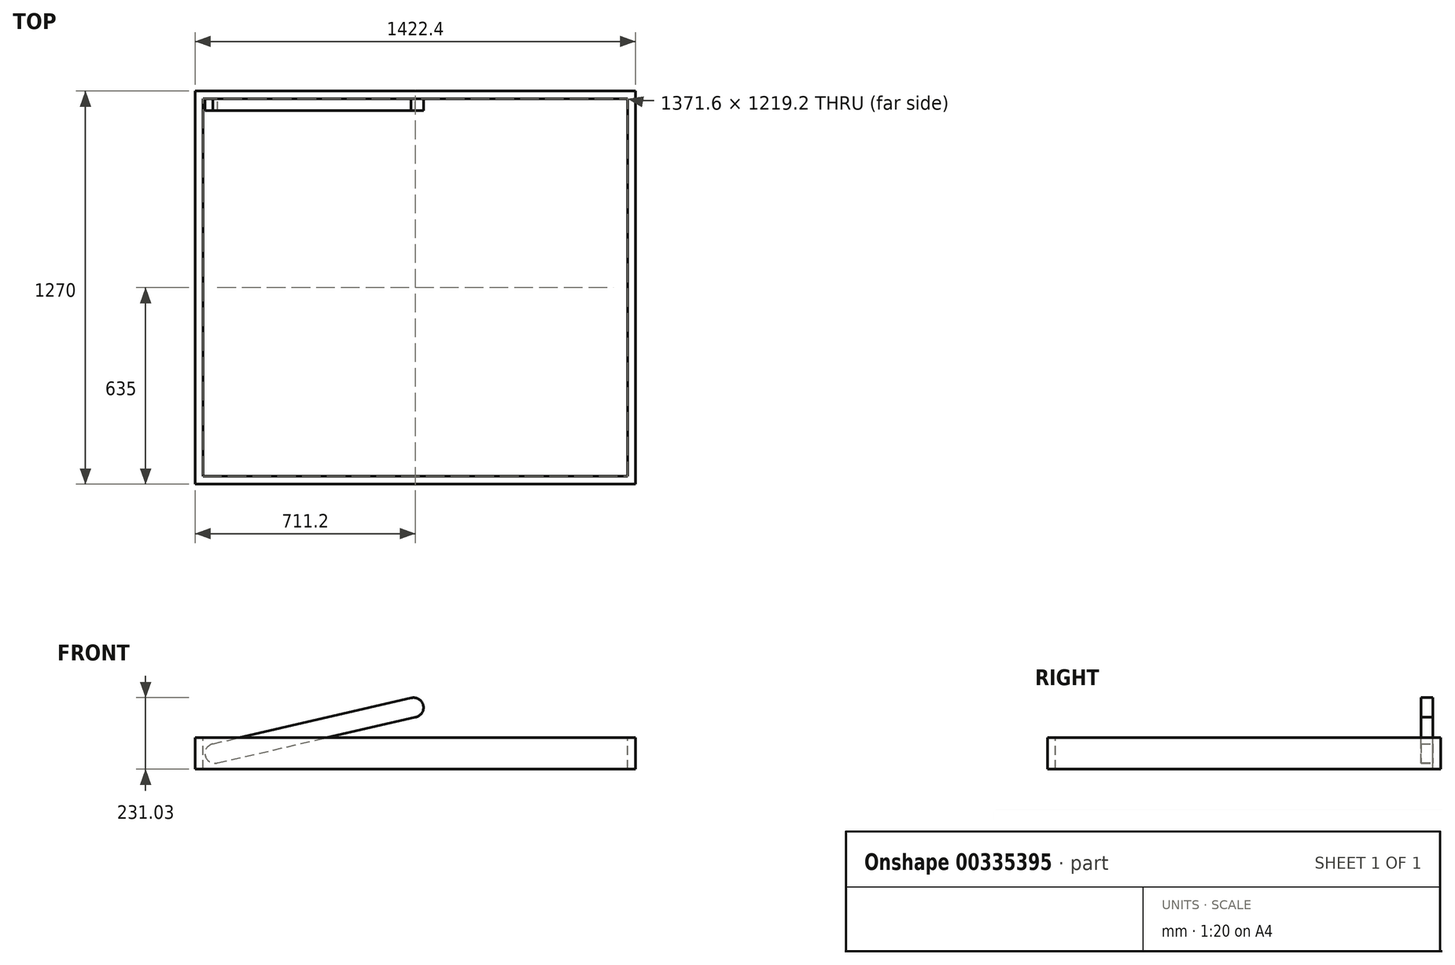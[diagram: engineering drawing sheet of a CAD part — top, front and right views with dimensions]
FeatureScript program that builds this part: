
annotation { "Feature Type Name" : "Feature", "Feature Type Description" : "" }
export const myFeature = defineFeature(function(context is Context, id is Id, definition is map)
    precondition{}
    {
        {
            var Q0;
            Q0=qCreatedBy(makeId("Top.planeOp"),FACE);
            var sketch = newSketch(context, id + "F0", { "sketchPlane" : qUnion([Q0])});
            skLineSegment(sketch, "E0.bottom", {"start": v(685.8, 609.6) * mm, "end": v(-685.8, 609.6) * mm});
            skLineSegment(sketch, "E0.top", {"start": v(685.8, -609.6) * mm, "end": v(-685.8, -609.6) * mm});
            skLineSegment(sketch, "E0.left", {"start": v(685.8, 609.6) * mm, "end": v(685.8, -609.6) * mm});
            skLineSegment(sketch, "E0.right", {"start": v(-685.8, 609.6) * mm, "end": v(-685.8, -609.6) * mm});
            skPoint(sketch, "E0.middle", {"position": v(0, 0) * mm});
            skSolve(sketch);
        }
        {
            var Q0;
            Q0=qCreatedBy(makeId("Front.planeOp"),FACE);
            cPlane(context, id + "F1", {"entities" : qUnion([Q0]), "cplaneType" : CPlaneType.OFFSET, "offset" : 609.6 * mm, "width" : 152.4 * mm, "height" : 152.4 * mm});
        }
        {
            var Q0;
            Q0=qCreatedBy(id+"F1.planeOp",FACE);
            var sketch = newSketch(context, id + "F2", { "sketchPlane" : qUnion([Q0])});
            skLineSegment(sketch, "E1.bottom", {"start": v(-685.8, 0) * mm, "end": v(711.2, 0) * mm});
            skLineSegment(sketch, "E1.top", {"start": v(-685.8, 101.6) * mm, "end": v(711.2, 101.6) * mm});
            skLineSegment(sketch, "E1.left", {"start": v(-685.8, 0) * mm, "end": v(-685.8, 101.6) * mm});
            skLineSegment(sketch, "E1.right", {"start": v(711.2, 0) * mm, "end": v(711.2, 101.6) * mm});
            skSolve(sketch);
        }
        {
            var Q0;
            Q0=qCreatedBy(makeId("Right.planeOp"),FACE);
            cPlane(context, id + "F3", {"entities" : qUnion([Q0]), "cplaneType" : CPlaneType.OFFSET, "offset" : 685.8 * mm, "width" : 152.4 * mm, "height" : 152.4 * mm});
        }
        {
            var Q0;
            Q0=qCreatedBy(id+"F3.planeOp",FACE);
            var sketch = newSketch(context, id + "F4", { "sketchPlane" : qUnion([Q0])});
            skLineSegment(sketch, "E2.bottom", {"start": v(-609.6, 0) * mm, "end": v(609.6, 0) * mm});
            skLineSegment(sketch, "E2.top", {"start": v(-609.6, 101.6) * mm, "end": v(609.6, 101.6) * mm});
            skLineSegment(sketch, "E2.left", {"start": v(-609.6, 0) * mm, "end": v(-609.6, 101.6) * mm});
            skLineSegment(sketch, "E2.right", {"start": v(609.6, 0) * mm, "end": v(609.6, 101.6) * mm});
            skSolve(sketch);
        }
        {
            var Q0;
            Q0=qCreatedBy(makeId("Front.planeOp"),FACE);
            cPlane(context, id + "F5", {"entities" : qUnion([Q0]), "cplaneType" : CPlaneType.OFFSET, "offset" : 609.6 * mm, "oppositeDirection" : true, "width" : 152.4 * mm, "height" : 152.4 * mm});
        }
        {
            var Q0;
            Q0=qCreatedBy(makeId("Right.planeOp"),FACE);
            cPlane(context, id + "F6", {"entities" : qUnion([Q0]), "cplaneType" : CPlaneType.OFFSET, "offset" : 685.8 * mm, "oppositeDirection" : true, "width" : 152.4 * mm, "height" : 152.4 * mm});
        }
        {
            var Q0;
            Q0=qCreatedBy(id+"F5.planeOp",FACE);
            var sketch = newSketch(context, id + "F7", { "sketchPlane" : qUnion([Q0])});
            skLineSegment(sketch, "E3.bottom", {"start": v(685.8, 0) * mm, "end": v(-685.8, 0) * mm});
            skLineSegment(sketch, "E3.top", {"start": v(685.8, 101.6) * mm, "end": v(-685.8, 101.6) * mm});
            skLineSegment(sketch, "E3.right", {"start": v(-685.8, 0) * mm, "end": v(-685.8, 101.6) * mm});
            skLineSegment(sketch, "E4", {"start": v(685.8, 0) * mm, "end": v(711.2, 0) * mm});
            skLineSegment(sketch, "E5", {"start": v(711.2, 0) * mm, "end": v(711.2, 101.6) * mm});
            skLineSegment(sketch, "E6", {"start": v(711.2, 101.6) * mm, "end": v(685.8, 101.6) * mm});
            skSolve(sketch);
        }
        {
            var Q0;
            Q0=qCreatedBy(id+"F6.planeOp",FACE);
            var sketch = newSketch(context, id + "F8", { "sketchPlane" : qUnion([Q0])});
            skLineSegment(sketch, "E7.bottom", {"start": v(635, 0) * mm, "end": v(-609.6, 0) * mm});
            skLineSegment(sketch, "E7.top", {"start": v(635, 101.6) * mm, "end": v(-609.6, 101.6) * mm});
            skLineSegment(sketch, "E7.left", {"start": v(635, 0) * mm, "end": v(635, 101.6) * mm});
            skLineSegment(sketch, "E8", {"start": v(-609.6, 0) * mm, "end": v(-635, 0) * mm});
            skLineSegment(sketch, "E9", {"start": v(-635, 0) * mm, "end": v(-635, 101.6) * mm});
            skLineSegment(sketch, "E10", {"start": v(-609.6, 101.6) * mm, "end": v(-635, 101.6) * mm});
            skSolve(sketch);
        }
        {
            var Q0;
            Q0=makeQuery(id+"F7.imprint","IMPRINT",FACE,{"disambiguationData":[TD([[makeQuery(id+"F7.imprint","IMPRINT",EDGE,{"derivedFrom":sQuery(id+"F7.wireOp",EDGE,"E3.bottom")}),-1.0]])]});
            var sketch = newSketch(context, id + "F9", { "sketchPlane" : qUnion([Q0])});
            skCircle(sketch, "E11", {"center": v(-647.7, 50.8) * mm, "radius": 31.75 * mm});
            skSolve(sketch);
        }
        {
            var Q0;
            Q0=qCreatedBy(id+"F5.planeOp",FACE);
            var sketch = newSketch(context, id + "F10", { "sketchPlane" : qUnion([Q0])});
            skLineSegment(sketch, "E12", {"start": v(-653.52, 82.01) * mm, "end": v(-639.23, 20.2) * mm});
            skCircle(sketch, "E13", {"center": v(-5.46, 199.28) * mm, "radius": 31.75 * mm});
            skLineSegment(sketch, "E14", {"start": v(-653.52, 82.01) * mm, "end": v(-13.93, 229.88) * mm});
            skLineSegment(sketch, "E15", {"start": v(-639.23, 20.2) * mm, "end": v(0.36, 168.07) * mm});
            skSolve(sketch);
        }
        {
            var Q0;
            Q0 = qSketchRegion(id + "F10", true);
            extrude(context, id + "F11", {"entities" : qUnion([Q0]), "depth" : 38.1 * mm});
        }
        {
            var Q0;
            Q0 = qSketchRegion(id + "F9", true);
            extrude(context, id + "F12", {"entities" : qUnion([Q0]), "operationType" : NewBodyOperationType.ADD, "depth" : 38.1 * mm});
        }
        {
            var Q0;
            Q0=makeQuery(id+"F12.boolean.opBoolean","MERGE",FACE,{"derivedFrom":[makeQuery(id+"F11.opExtrude","CAP_FACE",FACE,{"disambiguationData":[OSD([sQuery(id+"F10.wireOp",EDGE,"E12"),sQuery(id+"F10.wireOp",EDGE,"E13"),sQuery(id+"F10.wireOp",EDGE,"E14"),sQuery(id+"F10.wireOp",EDGE,"E15")])],"isStart":false}),makeQuery(id+"F12.opExtrude","CAP_FACE",FACE,{"disambiguationData":[OSD([sQuery(id+"F9.wireOp",EDGE,"E11")])],"isStart":false})]});
            var sketch = newSketch(context, id + "F13", { "sketchPlane" : qUnion([Q0])});
            skSolve(sketch);
        }
        {
            var Q0;
            Q0=makeQuery(id+"F4.imprint","IMPRINT",FACE,{"disambiguationData":[TD([[makeQuery(id+"F4.imprint","IMPRINT",EDGE,{"derivedFrom":sQuery(id+"F4.wireOp",EDGE,"E2.bottom")}),1.0]])]});
            extrude(context, id + "F14", {"entities" : qUnion([Q0]), "depth" : 25.4 * mm});
        }
        {
            var Q0;
            Q0=makeQuery(id+"F2.imprint","IMPRINT",FACE,{"disambiguationData":[TD([[makeQuery(id+"F2.imprint","IMPRINT",EDGE,{"derivedFrom":sQuery(id+"F2.wireOp",EDGE,"E1.bottom")}),1.0]])]});
            extrude(context, id + "F15", {"entities" : qUnion([Q0]), "operationType" : NewBodyOperationType.ADD, "depth" : 25.4 * mm});
        }
        {
            var Q0;
            Q0=makeQuery(id+"F8.imprint","IMPRINT",FACE,{"disambiguationData":[TD([[makeQuery(id+"F8.imprint","IMPRINT",EDGE,{"derivedFrom":sQuery(id+"F8.wireOp",EDGE,"E7.bottom")}),-1.0]])]});
            extrude(context, id + "F16", {"entities" : qUnion([Q0]), "operationType" : NewBodyOperationType.ADD, "oppositeDirection" : true, "depth" : 25.4 * mm});
        }
        {
            var Q0;
            Q0=makeQuery(id+"F7.imprint","IMPRINT",FACE,{"disambiguationData":[TD([[makeQuery(id+"F7.imprint","IMPRINT",EDGE,{"derivedFrom":sQuery(id+"F7.wireOp",EDGE,"E3.bottom")}),-1.0]])]});
            extrude(context, id + "F17", {"entities" : qUnion([Q0]), "operationType" : NewBodyOperationType.ADD, "oppositeDirection" : true, "depth" : 25.4 * mm});
        }
    });
